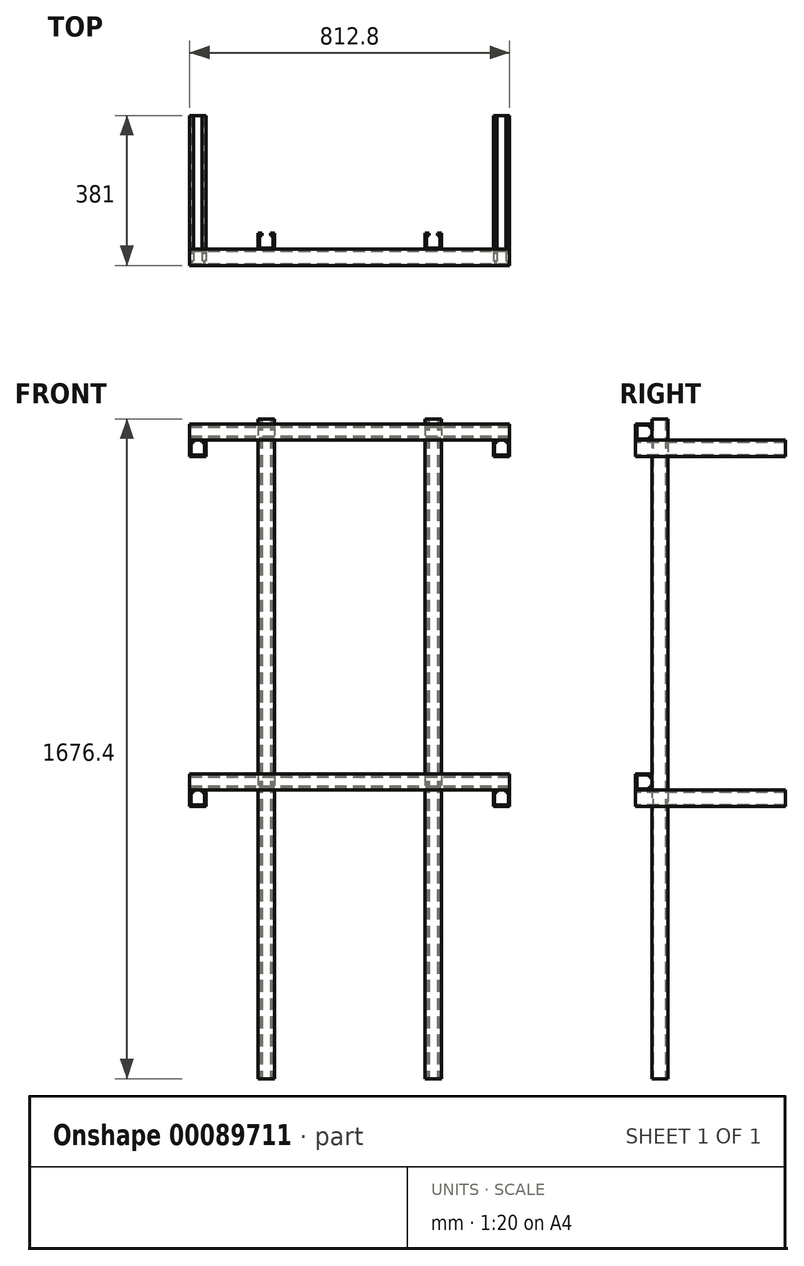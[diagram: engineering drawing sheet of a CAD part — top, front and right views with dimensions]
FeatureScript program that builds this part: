
annotation { "Feature Type Name" : "Feature", "Feature Type Description" : "" }
export const myFeature = defineFeature(function(context is Context, id is Id, definition is map)
    precondition{}
    {
        {
            var Q0;
            Q0=qCreatedBy(makeId("Top.planeOp"),FACE);
            var sketch = newSketch(context, id + "F0", { "sketchPlane" : qUnion([Q0])});
            skLineSegment(sketch, "E0", {"start": v(-232.73, -20.64) * mm, "end": v(-232.73, 20.64) * mm});
            skLineSegment(sketch, "E1", {"start": v(-232.73, 20.64) * mm, "end": v(-223.2, 20.64) * mm});
            skLineSegment(sketch, "E2", {"start": v(-223.2, 20.64) * mm, "end": v(-223.2, 14.29) * mm});
            skLineSegment(sketch, "E3", {"start": v(-229.55, 17.46) * mm, "end": v(-229.55, -17.46) * mm});
            skLineSegment(sketch, "E4", {"start": v(-229.55, -17.46) * mm, "end": v(-194.63, -17.46) * mm});
            skLineSegment(sketch, "E5", {"start": v(-194.63, -17.46) * mm, "end": v(-194.63, 17.46) * mm});
            skLineSegment(sketch, "E6", {"start": v(-200.98, 14.29) * mm, "end": v(-200.98, 20.64) * mm});
            skLineSegment(sketch, "E7", {"start": v(-200.98, 20.64) * mm, "end": v(-191.45, 20.64) * mm});
            skLineSegment(sketch, "E8", {"start": v(-191.45, 20.64) * mm, "end": v(-191.45, -20.64) * mm});
            skLineSegment(sketch, "E9", {"start": v(-191.45, -20.64) * mm, "end": v(-232.73, -20.64) * mm});
            skLineSegment(sketch, "E10", {"start": v(-223.2, 14.29) * mm, "end": v(-226.38, 14.29) * mm});
            skLineSegment(sketch, "E11", {"start": v(-229.55, 17.46) * mm, "end": v(-226.38, 17.46) * mm});
            skLineSegment(sketch, "E12", {"start": v(-226.38, 17.46) * mm, "end": v(-226.38, 14.29) * mm});
            skLineSegment(sketch, "E13", {"start": v(-200.98, 14.29) * mm, "end": v(-197.8, 14.29) * mm});
            skLineSegment(sketch, "E14", {"start": v(-197.8, 14.29) * mm, "end": v(-197.8, 17.46) * mm});
            skLineSegment(sketch, "E15", {"start": v(-197.8, 17.46) * mm, "end": v(-194.63, 17.46) * mm});
            skLineSegment(sketch, "E16", {"start": v(-232.73, 0) * mm, "end": v(-191.45, 0) * mm, "construction": true});
            skLineSegment(sketch, "E17", {"start": v(-212.1, -20.64) * mm, "end": v(-212.1, 0) * mm, "construction": true});
            skLineSegment(sketch, "E18.MirrorCS", {"start": v(197.8, 14.29) * mm, "end": v(197.8, 17.46) * mm});
            skLineSegment(sketch, "E19.MirrorCS", {"start": v(197.8, 17.46) * mm, "end": v(194.63, 17.46) * mm});
            skLineSegment(sketch, "E20.MirrorCS", {"start": v(200.98, 20.64) * mm, "end": v(191.45, 20.64) * mm});
            skLineSegment(sketch, "E21.MirrorCS", {"start": v(229.55, 17.46) * mm, "end": v(226.38, 17.46) * mm});
            skLineSegment(sketch, "E22.MirrorCS", {"start": v(226.38, 17.46) * mm, "end": v(226.38, 14.29) * mm});
            skLineSegment(sketch, "E23.MirrorCS", {"start": v(200.98, 14.29) * mm, "end": v(197.8, 14.29) * mm});
            skLineSegment(sketch, "E24.MirrorCS", {"start": v(232.73, 20.64) * mm, "end": v(223.2, 20.64) * mm});
            skLineSegment(sketch, "E25.MirrorCS", {"start": v(223.2, 20.64) * mm, "end": v(223.2, 14.29) * mm});
            skLineSegment(sketch, "E26.MirrorCS", {"start": v(200.98, 14.29) * mm, "end": v(200.98, 20.64) * mm});
            skLineSegment(sketch, "E27.MirrorCS", {"start": v(223.2, 14.29) * mm, "end": v(226.38, 14.29) * mm});
            skLineSegment(sketch, "E28.MirrorCS", {"start": v(212.1, -20.64) * mm, "end": v(212.1, 0) * mm, "construction": true});
            skLineSegment(sketch, "E29.MirrorCS", {"start": v(232.73, 0) * mm, "end": v(191.45, 0) * mm, "construction": true});
            skLineSegment(sketch, "E30.MirrorCS", {"start": v(232.73, -20.64) * mm, "end": v(232.73, 20.64) * mm});
            skLineSegment(sketch, "E31.MirrorCS", {"start": v(229.55, 17.46) * mm, "end": v(229.55, -17.46) * mm});
            skLineSegment(sketch, "E32.MirrorCS", {"start": v(229.55, -17.46) * mm, "end": v(194.63, -17.46) * mm});
            skLineSegment(sketch, "E33.MirrorCS", {"start": v(194.63, -17.46) * mm, "end": v(194.63, 17.46) * mm});
            skLineSegment(sketch, "E34.MirrorCS", {"start": v(191.45, 20.64) * mm, "end": v(191.45, -20.64) * mm});
            skLineSegment(sketch, "E35.MirrorCS", {"start": v(191.45, -20.64) * mm, "end": v(232.73, -20.64) * mm});
            skSolve(sketch);
        }
        {
            var Q0;
            Q0 = qSketchRegion(id + "F0", true);
            extrude(context, id + "F1", {"entities" : qUnion([Q0]), "endBound" : BoundingType.SYMMETRIC, "depth" : 1676.4 * mm});
        }
        {
            var Q0;
            Q0=qCreatedBy(makeId("Right.planeOp"),FACE);
            var sketch = newSketch(context, id + "F2", { "sketchPlane" : qUnion([Q0])});
            skLineSegment(sketch, "E36", {"start": v(-61.91, 825.5) * mm, "end": v(-61.91, 784.23) * mm});
            skLineSegment(sketch, "E37", {"start": v(-61.91, 784.23) * mm, "end": v(-20.64, 784.23) * mm});
            skLineSegment(sketch, "E38", {"start": v(-20.64, 784.22) * mm, "end": v(-20.64, 793.75) * mm});
            skLineSegment(sketch, "E39", {"start": v(-20.64, 793.75) * mm, "end": v(-26.99, 793.75) * mm});
            skLineSegment(sketch, "E40", {"start": v(-61.91, 825.5) * mm, "end": v(-20.64, 825.5) * mm});
            skLineSegment(sketch, "E41", {"start": v(-20.64, 825.5) * mm, "end": v(-20.64, 815.98) * mm});
            skLineSegment(sketch, "E42", {"start": v(-20.64, 815.98) * mm, "end": v(-26.99, 815.98) * mm});
            skLineSegment(sketch, "E43", {"start": v(-26.99, 815.98) * mm, "end": v(-26.99, 819.15) * mm});
            skLineSegment(sketch, "E44", {"start": v(-26.99, 819.15) * mm, "end": v(-23.81, 819.15) * mm});
            skLineSegment(sketch, "E45", {"start": v(-23.81, 819.15) * mm, "end": v(-23.81, 822.32) * mm});
            skLineSegment(sketch, "E46", {"start": v(-23.81, 822.32) * mm, "end": v(-58.74, 822.32) * mm});
            skLineSegment(sketch, "E47", {"start": v(-58.74, 822.32) * mm, "end": v(-58.74, 787.4) * mm});
            skLineSegment(sketch, "E48", {"start": v(-58.74, 787.4) * mm, "end": v(-23.81, 787.4) * mm});
            skLineSegment(sketch, "E49", {"start": v(-23.81, 787.4) * mm, "end": v(-23.81, 790.57) * mm});
            skLineSegment(sketch, "E50", {"start": v(-23.81, 790.57) * mm, "end": v(-26.99, 790.57) * mm});
            skLineSegment(sketch, "E51", {"start": v(-26.99, 790.57) * mm, "end": v(-26.99, 793.75) * mm});
            skLineSegment(sketch, "E52.0.1.0", {"start": v(-61.91, -63.5) * mm, "end": v(-20.64, -63.5) * mm});
            skLineSegment(sketch, "E52.0.1.1", {"start": v(-61.91, -63.5) * mm, "end": v(-61.91, -104.77) * mm});
            skLineSegment(sketch, "E52.0.1.2", {"start": v(-23.81, -66.68) * mm, "end": v(-58.74, -66.68) * mm});
            skLineSegment(sketch, "E52.0.1.3", {"start": v(-58.74, -66.68) * mm, "end": v(-58.74, -101.6) * mm});
            skLineSegment(sketch, "E52.0.1.4", {"start": v(-61.91, -104.77) * mm, "end": v(-20.64, -104.77) * mm});
            skLineSegment(sketch, "E52.0.1.5", {"start": v(-58.74, -101.6) * mm, "end": v(-23.81, -101.6) * mm});
            skLineSegment(sketch, "E52.0.1.6", {"start": v(-26.99, -98.43) * mm, "end": v(-26.99, -95.25) * mm});
            skLineSegment(sketch, "E52.0.1.7", {"start": v(-23.81, -98.43) * mm, "end": v(-26.99, -98.43) * mm});
            skLineSegment(sketch, "E52.0.1.8", {"start": v(-20.64, -104.78) * mm, "end": v(-20.64, -95.25) * mm});
            skLineSegment(sketch, "E52.0.1.9", {"start": v(-20.64, -95.25) * mm, "end": v(-26.99, -95.25) * mm});
            skLineSegment(sketch, "E52.0.1.10", {"start": v(-20.64, -73.02) * mm, "end": v(-26.99, -73.02) * mm});
            skLineSegment(sketch, "E52.0.1.11", {"start": v(-20.64, -63.5) * mm, "end": v(-20.64, -73.02) * mm});
            skLineSegment(sketch, "E52.0.1.12", {"start": v(-26.99, -69.85) * mm, "end": v(-23.81, -69.85) * mm});
            skLineSegment(sketch, "E52.0.1.13", {"start": v(-23.81, -69.85) * mm, "end": v(-23.81, -66.68) * mm});
            skLineSegment(sketch, "E52.0.1.14", {"start": v(-23.81, -101.6) * mm, "end": v(-23.81, -98.43) * mm});
            skLineSegment(sketch, "E52.0.1.15", {"start": v(-26.99, -73.02) * mm, "end": v(-26.99, -69.85) * mm});
            skLineSegment(sketch, "E52.direction1", {"start": v(-61.91, 825.5) * mm, "end": v(-36.51, 825.5) * mm, "construction": true});
            skLineSegment(sketch, "E52.direction2", {"start": v(-61.91, 825.5) * mm, "end": v(-61.91, -63.5) * mm, "construction": true});
            skSolve(sketch);
        }
        {
            var Q0;
            Q0 = qSketchRegion(id + "F2", true);
            extrude(context, id + "F3", {"entities" : qUnion([Q0]), "endBound" : BoundingType.SYMMETRIC, "depth" : 812.8 * mm});
        }
        {
            var Q0;
            Q0=makeQuery(id+"F3.opExtrude","SWEPT_FACE",FACE,{"disambiguationData":[OSD([sQuery(id+"F2.wireOp",EDGE,"E36")])]});
            var sketch = newSketch(context, id + "F4", { "sketchPlane" : qUnion([Q0])});
            skLineSegment(sketch, "E53.MirrorCS", {"start": v(-400.05, 777.88) * mm, "end": v(-400.05, 781.05) * mm});
            skLineSegment(sketch, "E54.MirrorCS", {"start": v(-400.05, 781.05) * mm, "end": v(-403.23, 781.05) * mm});
            skLineSegment(sketch, "E55.MirrorCS", {"start": v(-396.88, 784.23) * mm, "end": v(-406.4, 784.23) * mm});
            skLineSegment(sketch, "E56.MirrorCS", {"start": v(-368.3, 781.05) * mm, "end": v(-371.48, 781.05) * mm});
            skLineSegment(sketch, "E57.MirrorCS", {"start": v(-371.48, 781.05) * mm, "end": v(-371.48, 777.88) * mm});
            skLineSegment(sketch, "E58.MirrorCS", {"start": v(-396.88, 777.88) * mm, "end": v(-400.05, 777.88) * mm});
            skLineSegment(sketch, "E59.MirrorCS", {"start": v(-365.13, 784.23) * mm, "end": v(-374.65, 784.23) * mm});
            skLineSegment(sketch, "E60.MirrorCS", {"start": v(-374.65, 784.23) * mm, "end": v(-374.65, 777.88) * mm});
            skLineSegment(sketch, "E61.MirrorCS", {"start": v(-396.88, 777.88) * mm, "end": v(-396.88, 784.23) * mm});
            skLineSegment(sketch, "E62.MirrorCS", {"start": v(-374.65, 777.88) * mm, "end": v(-371.48, 777.88) * mm});
            skLineSegment(sketch, "E63.MirrorCS", {"start": v(-365.13, 742.95) * mm, "end": v(-365.13, 784.23) * mm});
            skLineSegment(sketch, "E64.MirrorCS", {"start": v(-368.3, 781.05) * mm, "end": v(-368.3, 746.13) * mm});
            skLineSegment(sketch, "E65.MirrorCS", {"start": v(-368.3, 746.12) * mm, "end": v(-403.22, 746.12) * mm});
            skLineSegment(sketch, "E66.MirrorCS", {"start": v(-403.23, 746.13) * mm, "end": v(-403.23, 781.05) * mm});
            skLineSegment(sketch, "E67.MirrorCS", {"start": v(-406.4, 784.23) * mm, "end": v(-406.4, 742.95) * mm});
            skLineSegment(sketch, "E68.MirrorCS", {"start": v(-406.4, 742.95) * mm, "end": v(-365.13, 742.95) * mm});
            skLineSegment(sketch, "E69.0.1.0", {"start": v(-406.4, -104.77) * mm, "end": v(-406.4, -146.05) * mm});
            skLineSegment(sketch, "E69.0.1.1", {"start": v(-406.4, -146.05) * mm, "end": v(-365.13, -146.05) * mm});
            skLineSegment(sketch, "E69.0.1.2", {"start": v(-365.13, -146.05) * mm, "end": v(-365.13, -104.77) * mm});
            skLineSegment(sketch, "E69.0.1.3", {"start": v(-368.3, -107.95) * mm, "end": v(-368.3, -142.87) * mm});
            skLineSegment(sketch, "E69.0.1.4", {"start": v(-368.3, -142.87) * mm, "end": v(-403.22, -142.87) * mm});
            skLineSegment(sketch, "E69.0.1.5", {"start": v(-403.23, -142.87) * mm, "end": v(-403.23, -107.95) * mm});
            skLineSegment(sketch, "E69.0.1.6", {"start": v(-396.88, -104.77) * mm, "end": v(-406.4, -104.77) * mm});
            skLineSegment(sketch, "E69.0.1.7", {"start": v(-368.3, -107.95) * mm, "end": v(-371.48, -107.95) * mm});
            skLineSegment(sketch, "E69.0.1.8", {"start": v(-371.48, -107.95) * mm, "end": v(-371.48, -111.12) * mm});
            skLineSegment(sketch, "E69.0.1.9", {"start": v(-365.13, -104.77) * mm, "end": v(-374.65, -104.77) * mm});
            skLineSegment(sketch, "E69.0.1.10", {"start": v(-374.65, -104.77) * mm, "end": v(-374.65, -111.12) * mm});
            skLineSegment(sketch, "E69.0.1.11", {"start": v(-374.65, -111.12) * mm, "end": v(-371.48, -111.12) * mm});
            skLineSegment(sketch, "E69.0.1.12", {"start": v(-400.05, -107.95) * mm, "end": v(-403.23, -107.95) * mm});
            skLineSegment(sketch, "E69.0.1.13", {"start": v(-396.88, -111.12) * mm, "end": v(-400.05, -111.12) * mm});
            skLineSegment(sketch, "E69.0.1.14", {"start": v(-396.88, -111.12) * mm, "end": v(-396.88, -104.77) * mm});
            skLineSegment(sketch, "E69.0.1.15", {"start": v(-400.05, -111.12) * mm, "end": v(-400.05, -107.95) * mm});
            skLineSegment(sketch, "E69.1.0.0", {"start": v(365.13, 784.23) * mm, "end": v(365.13, 742.95) * mm});
            skLineSegment(sketch, "E69.1.0.1", {"start": v(365.13, 742.95) * mm, "end": v(406.4, 742.95) * mm});
            skLineSegment(sketch, "E69.1.0.2", {"start": v(406.4, 742.95) * mm, "end": v(406.4, 784.23) * mm});
            skLineSegment(sketch, "E69.1.0.3", {"start": v(403.23, 781.05) * mm, "end": v(403.23, 746.13) * mm});
            skLineSegment(sketch, "E69.1.0.4", {"start": v(403.23, 746.12) * mm, "end": v(368.3, 746.12) * mm});
            skLineSegment(sketch, "E69.1.0.5", {"start": v(368.3, 746.13) * mm, "end": v(368.3, 781.05) * mm});
            skLineSegment(sketch, "E69.1.0.6", {"start": v(374.65, 784.23) * mm, "end": v(365.13, 784.23) * mm});
            skLineSegment(sketch, "E69.1.0.7", {"start": v(403.23, 781.05) * mm, "end": v(400.05, 781.05) * mm});
            skLineSegment(sketch, "E69.1.0.8", {"start": v(400.05, 781.05) * mm, "end": v(400.05, 777.88) * mm});
            skLineSegment(sketch, "E69.1.0.9", {"start": v(406.4, 784.23) * mm, "end": v(396.88, 784.23) * mm});
            skLineSegment(sketch, "E69.1.0.10", {"start": v(396.88, 784.23) * mm, "end": v(396.88, 777.88) * mm});
            skLineSegment(sketch, "E69.1.0.11", {"start": v(396.88, 777.88) * mm, "end": v(400.05, 777.88) * mm});
            skLineSegment(sketch, "E69.1.0.12", {"start": v(371.48, 781.05) * mm, "end": v(368.3, 781.05) * mm});
            skLineSegment(sketch, "E69.1.0.13", {"start": v(374.65, 777.88) * mm, "end": v(371.48, 777.88) * mm});
            skLineSegment(sketch, "E69.1.0.14", {"start": v(374.65, 777.88) * mm, "end": v(374.65, 784.23) * mm});
            skLineSegment(sketch, "E69.1.0.15", {"start": v(371.48, 777.88) * mm, "end": v(371.48, 781.05) * mm});
            skLineSegment(sketch, "E69.1.1.0", {"start": v(365.13, -104.77) * mm, "end": v(365.13, -146.05) * mm});
            skLineSegment(sketch, "E69.1.1.1", {"start": v(365.13, -146.05) * mm, "end": v(406.4, -146.05) * mm});
            skLineSegment(sketch, "E69.1.1.2", {"start": v(406.4, -146.05) * mm, "end": v(406.4, -104.77) * mm});
            skLineSegment(sketch, "E69.1.1.3", {"start": v(403.23, -107.95) * mm, "end": v(403.23, -142.87) * mm});
            skLineSegment(sketch, "E69.1.1.4", {"start": v(403.23, -142.87) * mm, "end": v(368.3, -142.87) * mm});
            skLineSegment(sketch, "E69.1.1.5", {"start": v(368.3, -142.87) * mm, "end": v(368.3, -107.95) * mm});
            skLineSegment(sketch, "E69.1.1.6", {"start": v(374.65, -104.77) * mm, "end": v(365.13, -104.77) * mm});
            skLineSegment(sketch, "E69.1.1.7", {"start": v(403.23, -107.95) * mm, "end": v(400.05, -107.95) * mm});
            skLineSegment(sketch, "E69.1.1.8", {"start": v(400.05, -107.95) * mm, "end": v(400.05, -111.12) * mm});
            skLineSegment(sketch, "E69.1.1.9", {"start": v(406.4, -104.77) * mm, "end": v(396.88, -104.77) * mm});
            skLineSegment(sketch, "E69.1.1.10", {"start": v(396.88, -104.77) * mm, "end": v(396.88, -111.12) * mm});
            skLineSegment(sketch, "E69.1.1.11", {"start": v(396.88, -111.12) * mm, "end": v(400.05, -111.12) * mm});
            skLineSegment(sketch, "E69.1.1.12", {"start": v(371.48, -107.95) * mm, "end": v(368.3, -107.95) * mm});
            skLineSegment(sketch, "E69.1.1.13", {"start": v(374.65, -111.12) * mm, "end": v(371.48, -111.12) * mm});
            skLineSegment(sketch, "E69.1.1.14", {"start": v(374.65, -111.12) * mm, "end": v(374.65, -104.77) * mm});
            skLineSegment(sketch, "E69.1.1.15", {"start": v(371.48, -111.12) * mm, "end": v(371.48, -107.95) * mm});
            skLineSegment(sketch, "E69.direction1", {"start": v(-406.4, 742.95) * mm, "end": v(365.13, 742.95) * mm, "construction": true});
            skLineSegment(sketch, "E69.direction2", {"start": v(-406.4, 742.95) * mm, "end": v(-406.4, -146.05) * mm, "construction": true});
            skSolve(sketch);
        }
        {
            var Q0;
            Q0 = qSketchRegion(id + "F4", true);
            extrude(context, id + "F5", {"entities" : qUnion([Q0]), "oppositeDirection" : true, "depth" : 381 * mm});
        }
    });
